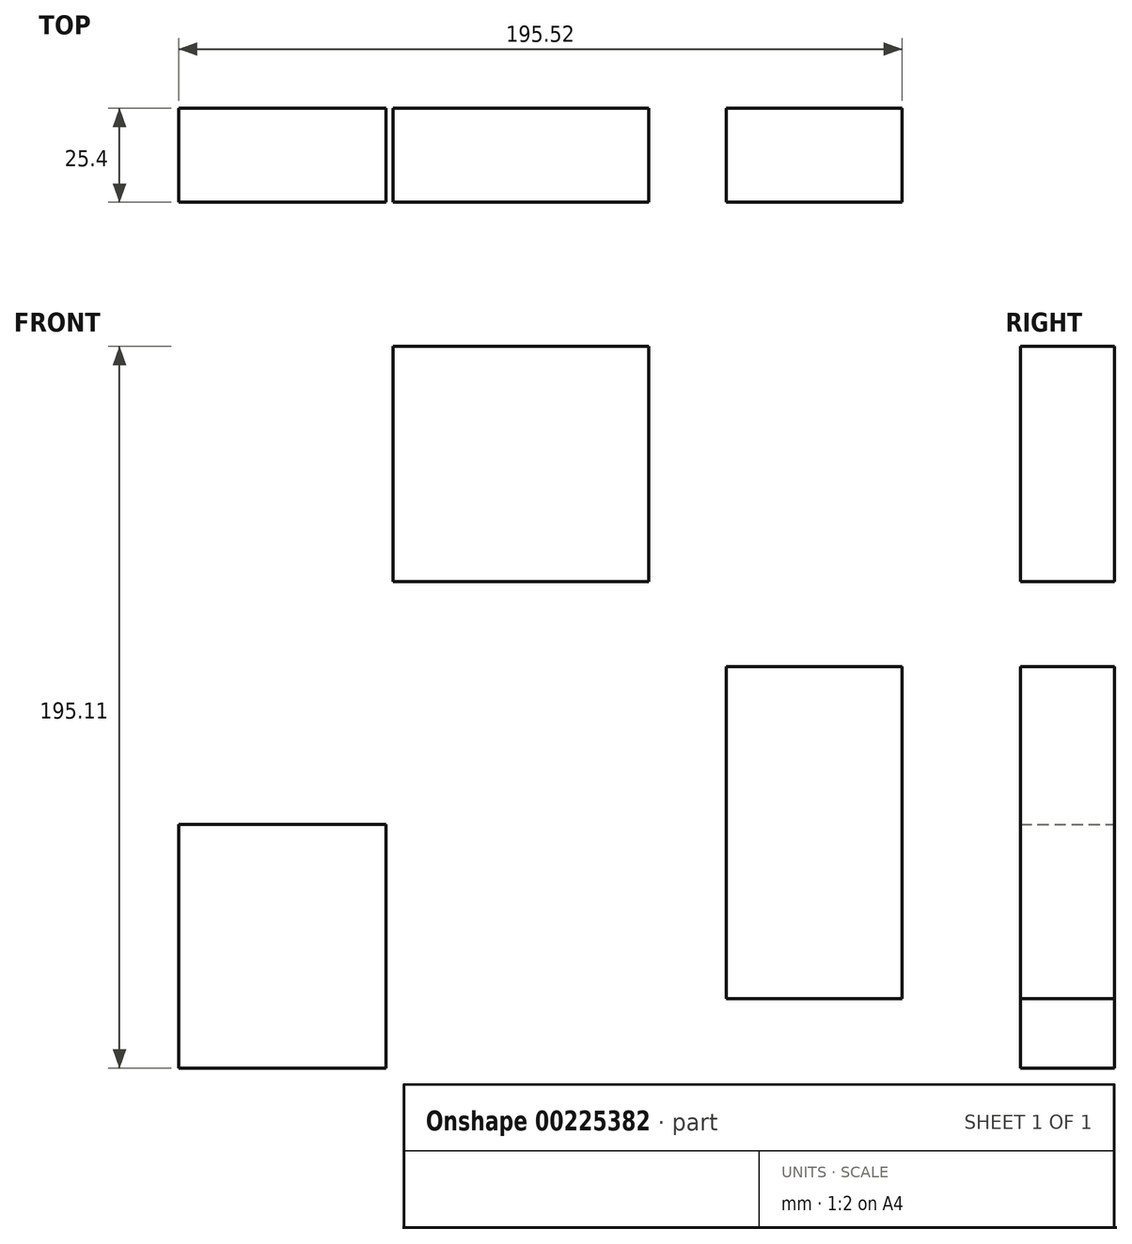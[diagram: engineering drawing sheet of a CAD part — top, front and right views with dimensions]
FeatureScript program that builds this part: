
annotation { "Feature Type Name" : "Feature", "Feature Type Description" : "" }
export const myFeature = defineFeature(function(context is Context, id is Id, definition is map)
    precondition{}
    {
        {
            var Q0;
            Q0=qCreatedBy(makeId("Front.planeOp"),FACE);
            var sketch = newSketch(context, id + "F0", { "sketchPlane" : qUnion([Q0])});
            skLineSegment(sketch, "E0.bottom", {"start": v(-48, 100.66) * mm, "end": v(21, 100.66) * mm});
            skLineSegment(sketch, "E0.top", {"start": v(-48, 37.07) * mm, "end": v(21, 37.07) * mm});
            skLineSegment(sketch, "E0.left", {"start": v(-48, 100.66) * mm, "end": v(-48, 37.07) * mm});
            skLineSegment(sketch, "E0.right", {"start": v(21, 100.66) * mm, "end": v(21, 37.07) * mm});
            skLineSegment(sketch, "E1.bottom", {"start": v(-106.01, -28.6) * mm, "end": v(-50, -28.6) * mm});
            skLineSegment(sketch, "E1.top", {"start": v(-106.01, -94.45) * mm, "end": v(-50, -94.45) * mm});
            skLineSegment(sketch, "E1.left", {"start": v(-106.01, -28.6) * mm, "end": v(-106.01, -94.45) * mm});
            skLineSegment(sketch, "E1.right", {"start": v(-50, -28.6) * mm, "end": v(-50, -94.45) * mm});
            skLineSegment(sketch, "E2.bottom", {"start": v(42, 14.13) * mm, "end": v(89.51, 14.13) * mm});
            skLineSegment(sketch, "E2.top", {"start": v(42, -75.67) * mm, "end": v(89.51, -75.67) * mm});
            skLineSegment(sketch, "E2.left", {"start": v(42, 14.13) * mm, "end": v(42, -75.67) * mm});
            skLineSegment(sketch, "E2.right", {"start": v(89.51, 14.13) * mm, "end": v(89.51, -75.67) * mm});
            skSolve(sketch);
        }
        {
            var Q0;
            Q0=qSketchRegion(id+"F0",true);
            extrude(context, id + "F1", {"entities" : qUnion([Q0]), "depth" : 25.4 * mm});
        }
    });
